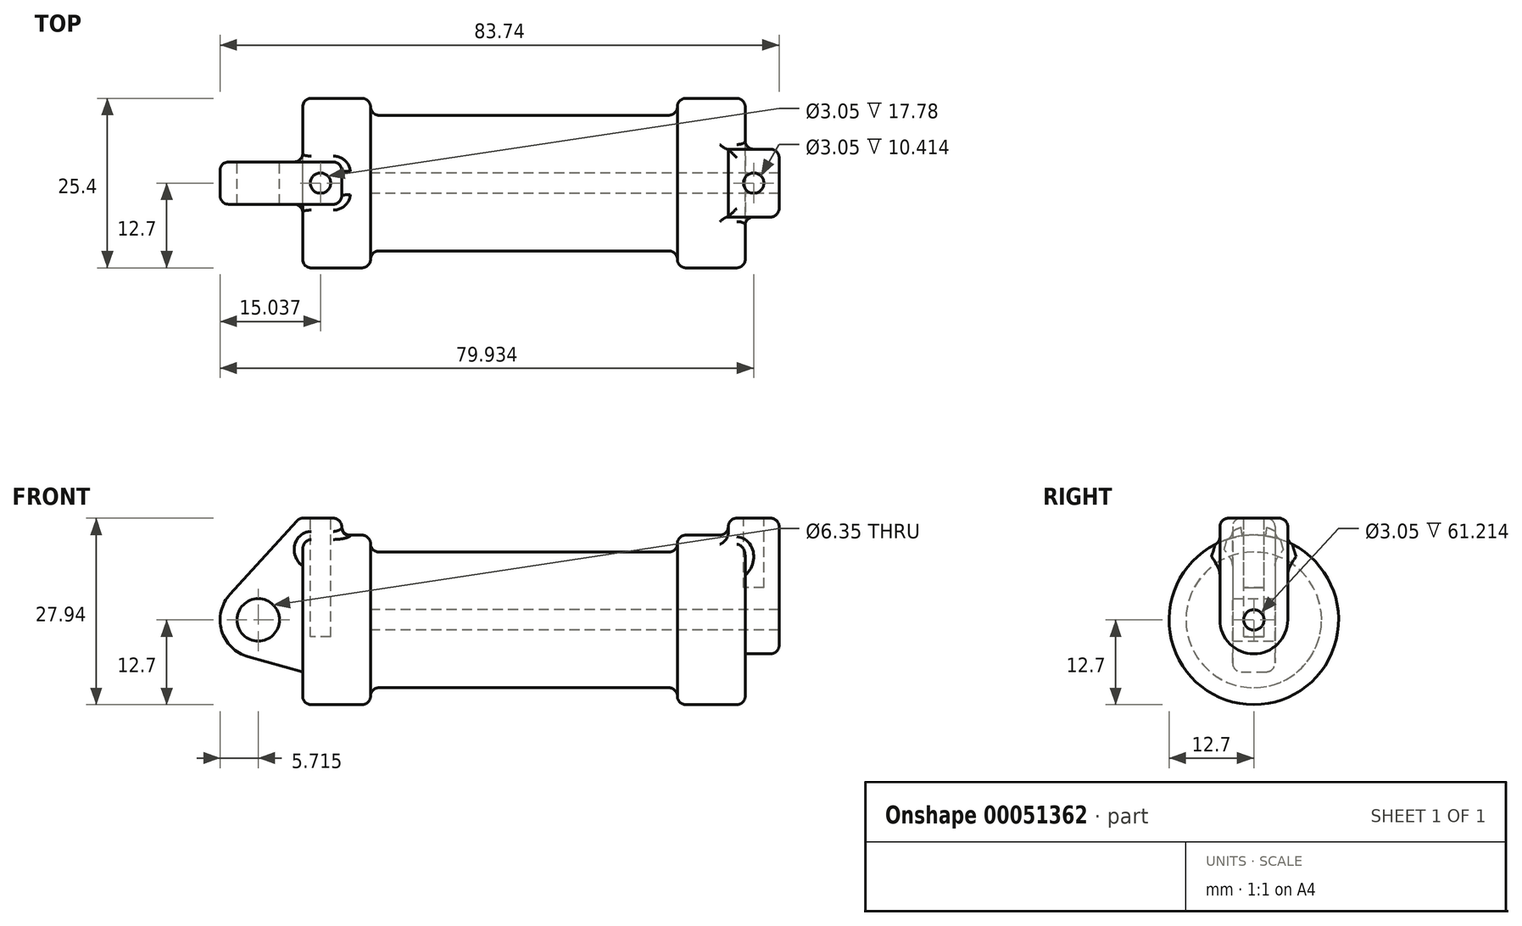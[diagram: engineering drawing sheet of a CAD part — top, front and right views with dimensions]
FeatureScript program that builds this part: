
annotation { "Feature Type Name" : "Feature", "Feature Type Description" : "" }
export const myFeature = defineFeature(function(context is Context, id is Id, definition is map)
    precondition{}
    {
        {
            var Q0;
            Q0=qCreatedBy(makeId("Front.planeOp"),FACE);
            var sketch = newSketch(context, id + "F0", { "sketchPlane" : qUnion([Q0])});
            skLineSegment(sketch, "E0", {"start": v(0, 0) * mm, "end": v(0, 12.7) * mm});
            skLineSegment(sketch, "E1", {"start": v(0, 12.7) * mm, "end": v(10.16, 12.7) * mm});
            skLineSegment(sketch, "E2", {"start": v(10.16, 12.7) * mm, "end": v(10.16, 10.16) * mm});
            skLineSegment(sketch, "E3", {"start": v(10.16, 10.16) * mm, "end": v(56.13, 10.16) * mm});
            skLineSegment(sketch, "E4", {"start": v(56.13, 10.16) * mm, "end": v(56.13, 12.7) * mm});
            skLineSegment(sketch, "E5", {"start": v(56.13, 12.7) * mm, "end": v(66.3, 12.7) * mm});
            skLineSegment(sketch, "E6", {"start": v(66.3, 12.7) * mm, "end": v(66.3, 0) * mm});
            skLineSegment(sketch, "E7", {"start": v(66.3, 0) * mm, "end": v(0, 0) * mm});
            skLineSegment(sketch, "E8", {"start": v(5.84, 15.24) * mm, "end": v(-0.5, 15.24) * mm});
            skLineSegment(sketch, "E9", {"start": v(-0.5, 15.24) * mm, "end": v(-10.88, 3.85) * mm});
            skLineSegment(sketch, "E10", {"start": v(0, 0) * mm, "end": v(-6.65, 0) * mm});
            skCircle(sketch, "E11", {"center": v(-6.65, 0) * mm, "radius": 5.72 * mm});
            skCircle(sketch, "E12", {"center": v(-6.65, 0) * mm, "radius": 3.18 * mm});
            skLineSegment(sketch, "E13", {"start": v(5.84, 15.24) * mm, "end": v(5.84, -9.4) * mm});
            skLineSegment(sketch, "E14", {"start": v(5.84, -9.4) * mm, "end": v(-8.18, -5.5) * mm});
            skSolve(sketch);
        }
        {
            var Q0;
            {var subQ0=sQuery(id+"F0.wireOp",EDGE,"E2");Q0=makeQuery(id+"F0.imprint","IMPRINT",FACE,{"disambiguationData":[TD([[makeQuery(id+"F0.imprint","IMPRINT",EDGE,{"derivedFrom":subQ0}),-1.0]])]});}
            var Q1;
            {var subQ0=sQuery(id+"F0.wireOp",EDGE,"E0");Q1=makeQuery(id+"F0.imprint","IMPRINT",FACE,{"disambiguationData":[TD([[makeQuery(id+"F0.imprint","IMPRINT",EDGE,{"derivedFrom":subQ0}),-1.0]])]});}
            var Q2;
            Q2=sQuery(id+"F0.wireOp",EDGE,"E7");
            revolve(context, id + "F1", {"entities" : qUnion([Q0, Q1]), "axis" : qUnion([Q2]), "revolveType" : RevolveType.FULL});
        }
        {
            var Q0;
            {var subQ0=sQuery(id+"F0.wireOp",EDGE,"E0");Q0=makeQuery(id+"F0.imprint","IMPRINT",FACE,{"disambiguationData":[TD([[makeQuery(id+"F0.imprint","IMPRINT",EDGE,{"derivedFrom":subQ0}),-1.0]])]});}
            var Q1;
            {var subQ3=sQuery(id+"F0.wireOp",EDGE,"E0");Q1=makeQuery(id+"F0.imprint","IMPRINT",FACE,{"disambiguationData":[TD([[makeQuery(id+"F0.imprint","IMPRINT",EDGE,{"derivedFrom":subQ3}),1.0]])]});}
            var Q2;
            {var subQ0=sQuery(id+"F0.wireOp",EDGE,"E14");Q2=makeQuery(id+"F0.imprint","IMPRINT",FACE,{"disambiguationData":[TD([[makeQuery(id+"F0.imprint","IMPRINT",EDGE,{"derivedFrom":subQ0}),-1.0]])]});}
            var Q3;
            {var subQ4=sQuery(id+"F0.wireOp",EDGE,"E12");Q3=makeQuery(id+"F0.imprint","IMPRINT",FACE,{"disambiguationData":[TD([[makeQuery(id+"F0.imprint","IMPRINT",EDGE,{"derivedFrom":subQ4}),-1.0]])]});}
            extrude(context, id + "F2", {"entities" : qUnion([Q0, Q1, Q2, Q3]), "operationType" : NewBodyOperationType.ADD, "endBound" : BoundingType.SYMMETRIC, "depth" : 6.35 * mm});
        }
        {
            var Q0;
            Q0=makeQuery(id+"F1.opRevolve","SWEPT_FACE",FACE,{"disambiguationData":[OSD([sQuery(id+"F0.wireOp",EDGE,"E6")])]});
            var sketch = newSketch(context, id + "F3", { "sketchPlane" : qUnion([Q0])});
            skCircle(sketch, "E15", {"center": v(0, 0) * mm, "radius": 1.52 * mm});
            skCircle(sketch, "E16", {"center": v(0, 0) * mm, "radius": 5.08 * mm});
            skLineSegment(sketch, "E17", {"start": v(-5.08, 0) * mm, "end": v(-5.08, 15.24) * mm});
            skLineSegment(sketch, "E18", {"start": v(5.08, 0) * mm, "end": v(5.08, 15.24) * mm});
            skLineSegment(sketch, "E19", {"start": v(-5.08, 15.24) * mm, "end": v(5.08, 15.24) * mm});
            skSolve(sketch);
        }
        {
            var Q0;
            Q0 = qSketchRegion(id + "F3", true);
            extrude(context, id + "F4", {"entities" : qUnion([Q0]), "operationType" : NewBodyOperationType.ADD, "oppositeDirection" : true, "depth" : 2.54 * mm});
        }
        {
            var Q0;
            Q0 = qSketchRegion(id + "F3", true);
            extrude(context, id + "F5", {"entities" : qUnion([Q0]), "operationType" : NewBodyOperationType.ADD, "depth" : 5.08 * mm});
        }
        {
            var Q0;
            Q0=makeQuery(id+"F3.imprint","IMPRINT",FACE,{"disambiguationData":[TD([[makeQuery(id+"F3.imprint","IMPRINT",EDGE,{"derivedFrom":sQuery(id+"F3.wireOp",EDGE,"E15")}),1.0]])]});
            var Q1;
            Q1=makeQuery(id+"F1.opRevolve","SWEPT_FACE",FACE,{"disambiguationData":[OSD([sQuery(id+"F0.wireOp",EDGE,"E2")])]});
            extrude(context, id + "F6", {"entities" : qUnion([Q0]), "operationType" : NewBodyOperationType.REMOVE, "endBound" : BoundingType.UP_TO_SURFACE, "oppositeDirection" : true, "endBoundEntityFace" : qUnion([Q1]), "depth" : 25.4 * mm});
        }
        {
            var Q0;
            {var subQ0=sQuery(id+"F3.wireOp",EDGE,"E19");Q0=makeQuery(id+"F5.boolean.opBoolean","MERGE",FACE,{"derivedFrom":[makeQuery(id+"F4.opExtrude","SWEPT_FACE",FACE,{"disambiguationData":[OSD([subQ0])]}),makeQuery(id+"F5.opExtrude","SWEPT_FACE",FACE,{"disambiguationData":[OSD([subQ0])]})]});}
            var sketch = newSketch(context, id + "F7", { "sketchPlane" : qUnion([Q0])});
            skCircle(sketch, "E20", {"center": v(67.56, 0) * mm, "radius": 1.52 * mm});
            skPoint(sketch, "E20.centerSnap0", {"position": v(63.75, 0) * mm});
            skPoint(sketch, "E20.centerSnap1", {"position": v(67.56, 5.08) * mm});
            skSolve(sketch);
        }
        {
            var Q0;
            Q0=makeQuery(id+"F2.opExtrude","SWEPT_FACE",FACE,{"disambiguationData":[OSD([sQuery(id+"F0.wireOp",EDGE,"E8")])]});
            var sketch = newSketch(context, id + "F8", { "sketchPlane" : qUnion([Q0])});
            skCircle(sketch, "E21", {"center": v(2.67, 0) * mm, "radius": 1.52 * mm});
            skPoint(sketch, "E21.centerSnap0", {"position": v(-0.5, 0) * mm});
            skPoint(sketch, "E21.centerSnap1", {"position": v(2.67, 3.18) * mm});
            skSolve(sketch);
        }
        {
            var Q0;
            Q0=makeQuery(id+"F8.imprint","IMPRINT",FACE,{"disambiguationData":[TD([[makeQuery(id+"F8.imprint","IMPRINT",EDGE,{"derivedFrom":sQuery(id+"F8.wireOp",EDGE,"E21")}),1.0]])]});
            extrude(context, id + "F9", {"entities" : qUnion([Q0]), "operationType" : NewBodyOperationType.REMOVE, "oppositeDirection" : true, "depth" : 17.78 * mm});
        }
        {
            var Q0;
            Q0=makeQuery(id+"F7.imprint","IMPRINT",FACE,{"disambiguationData":[TD([[makeQuery(id+"F7.imprint","IMPRINT",EDGE,{"derivedFrom":sQuery(id+"F7.wireOp",EDGE,"E20")}),1.0]])]});
            extrude(context, id + "F10", {"entities" : qUnion([Q0]), "operationType" : NewBodyOperationType.REMOVE, "oppositeDirection" : true, "depth" : 10.4 * mm});
        }
        {
            var Q0;
            Q0=makeQuery(id+"F1.opRevolve","SWEPT_FACE",FACE,{"disambiguationData":[OSD([sQuery(id+"F0.wireOp",EDGE,"E3")])]});
            var Q1;
            Q1=makeQuery(id+"F1.opRevolve","SWEPT_FACE",FACE,{"disambiguationData":[OSD([sQuery(id+"F0.wireOp",EDGE,"E5")])]});
            var Q2;
            Q2=makeQuery(id+"F1.opRevolve","SWEPT_FACE",FACE,{"disambiguationData":[OSD([sQuery(id+"F0.wireOp",EDGE,"E1")])]});
            var Q3;
            Q3=makeQuery(id+"F2.opExtrude","SWEPT_FACE",FACE,{"disambiguationData":[OSD([sQuery(id+"F0.wireOp",EDGE,"E13")])]});
            var Q4;
            Q4=makeQuery(id+"F2.opExtrude","CAP_EDGE",EDGE,{"disambiguationData":[OSD([sQuery(id+"F0.wireOp",EDGE,"E8")])],"isStart":false});
            var Q5;
            Q5=makeQuery(id+"F2.opExtrude","CAP_EDGE",EDGE,{"disambiguationData":[OSD([sQuery(id+"F0.wireOp",EDGE,"E8")])],"isStart":true});
            var Q6;
            Q6=makeQuery(id+"F2.opExtrude","SWEPT_EDGE",EDGE,{"disambiguationData":[OSD([sQuery(id+"F0.wireOp",EDGE,"E8"),sQuery(id+"F0.wireOp",EDGE,"E9")])]});
            var Q7;
            Q7=makeQuery(id+"F2.opExtrude","SWEPT_FACE",FACE,{"disambiguationData":[OSD([sQuery(id+"F0.wireOp",EDGE,"E9")])]});
            var Q8;
            Q8=makeQuery(id+"F5.opExtrude","CAP_EDGE",EDGE,{"disambiguationData":[OSD([sQuery(id+"F3.wireOp",EDGE,"E17")])],"isStart":false});
            var Q9;
            Q9=makeQuery(id+"F4.opExtrude","CAP_EDGE",EDGE,{"disambiguationData":[OSD([sQuery(id+"F3.wireOp",EDGE,"E19")])],"isStart":false});
            var Q10;
            {var subQ0=sQuery(id+"F3.wireOp",EDGE,"E19");var subQ1=sQuery(id+"F3.wireOp",EDGE,"E17");Q10=makeQuery(id+"F5.boolean.opBoolean","MERGE",EDGE,{"derivedFrom":[makeQuery(id+"F4.opExtrude","SWEPT_EDGE",EDGE,{"disambiguationData":[OSD([subQ1,subQ0])]}),makeQuery(id+"F5.opExtrude","SWEPT_EDGE",EDGE,{"disambiguationData":[OSD([subQ1,subQ0])]})]});}
            var Q11;
            {var subQ0=sQuery(id+"F3.wireOp",EDGE,"E19");var subQ1=sQuery(id+"F3.wireOp",EDGE,"E18");Q11=makeQuery(id+"F5.boolean.opBoolean","MERGE",EDGE,{"derivedFrom":[makeQuery(id+"F4.opExtrude","SWEPT_EDGE",EDGE,{"disambiguationData":[OSD([subQ1,subQ0])]}),makeQuery(id+"F5.opExtrude","SWEPT_EDGE",EDGE,{"disambiguationData":[OSD([subQ1,subQ0])]})]});}
            var Q12;
            Q12=makeQuery(id+"F5.opExtrude","CAP_EDGE",EDGE,{"disambiguationData":[OSD([sQuery(id+"F3.wireOp",EDGE,"E19")])],"isStart":false});
            fillet(context, id + "F11", {"entities" : qUnion([Q0, Q1, Q2, Q3, Q4, Q5, Q6, Q7, Q8, Q9, Q10, Q11, Q12]), "radius" : 1.27 * mm, "tangentPropagation" : true, "allowEdgeOverflow" : false});
        }
    });
